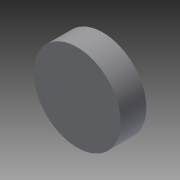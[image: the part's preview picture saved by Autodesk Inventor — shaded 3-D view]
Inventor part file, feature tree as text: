
AUTODESK INVENTOR PART (.ipt)
format: ipt  version: 2013 (Build 170138000, 138)  size: 70,656 bytes
history: native  units: in
note: dims shown in document units (in); Inventor stores cm internally (conversion verified against a paired STEP export)
features: extrude x1, sketch x1
ambient origin geometry x8: Origin, YZ Plane, XZ Plane, XY Plane, X Axis, Y Axis, Z Axis, Center Point
bodies: Solid1 (feature_tree)
feature tree (2):
  extrude  "Extrusion1"  Depth=0.3125in TaperAngle=0.0deg
  sketch  "Sketch1"  dims[d0=1.0625in d2=0.3125in d3=0.0in]
